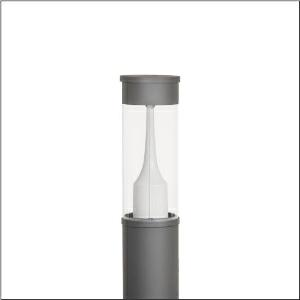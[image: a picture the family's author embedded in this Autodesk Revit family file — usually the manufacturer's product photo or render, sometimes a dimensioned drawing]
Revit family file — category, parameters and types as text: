
# Revit family: city-light_120_iq___pl1_2s_5xa5285rf14h_2286
name_source: partatom
category: Lighting Fixtures
units: mm (PartAtom-declared; Revit-internal decimal feet)

## family parameters
Cut with Voids When Loaded = No
Host = Face
Light Source = No
Part Type = Normal
Room Calculation Point = No
Round Connector Dimension = Use Diameter
Shared = No

## types (1)
- --- (1 x LED, 2970 lm, 18.5 W, 4000K)
    Apparent Load = 19 VA
    CIE Flux Codes = 23 62 94 96 100
    Color Rendering = 70
    Color Temperature = 4000K
    Default Elevation = 1800 mm
    Description = City-Light 120 iQ, bollard luminaire, Module 540 iQ-SR, primary light control with 3 zone facetted reflector, of plastic, silver coated, highly specular, structured, primary optical cover: cover, of PMMA, transparent, partly coated, light distribution: PL1.2s, primary light characteristic: symmetric, LED, High Power LED, rated luminous flux: 2.970lm, luminous efficacy: 161lm/W, light colour: 740, colour temperature: 4000K, control gear: iQ Street-Remote, control: pre-setting: logarithmic dimming characteristic, Street-Remote, Auto-Match, Temp-Guard, Lumen-Switch, Night-Set, Smart-Wire, Light-Fading, Desk-Remote (wireless, voltage-free reading and setting of iQ features in the workshop via application-optimized NFC function/RFID function), optimised constant luminous flux control (CLO 2.0), with terminal, 6-pole, max. 2.5mm², mains connection: 230..240V, AC, 50/60Hz, start of lifetime: 19W, end of service life: 20W, reduction: 9W, luminaire housing, cylindrical, of extruded aluminium section, coated, Siteco® metallic grey (DB 702S), length: 1.200mm, diameter: 200mm, Module 540 iQ-SR, traffic white (RAL 9016), equipment: standard, protection rating (complete): IP54, insulation class (complete): insulation class II (safety insulation), certification: CE, ENEC, VDE, packaging unit: 1 piece

Light Distribution: PL1.2s
    Height = 500 mm
    Lamp = 1 x LED
    Lamp Light Flux = 2970 lm
    Lamp Power = 18.5 W
    Lamp count = 1
    Length = 200 mm  [stored 0.656168 ft]
    Luminous efficacy = 161 lm/W
    Manufacturer = Siteco
    ModVariant = No
    Model = 5XA5285RF14H
    Mounting Place = Floor
    Mounting Type = Freestanding
    Number of Poles = 1
    OnlyDefault = Yes
    Power Factor = 1
    Product Name = City-Light 120 iQ | PL1.2s
    Product group = bollard luminaire
    ProductGroupID = 1304
    Protection Class = Protection class II
    Protection Degree = IP 54
    RLX_Detail_Level = 1
    RLX_Emergency_Light_Flux = 0 lm
    RLX_Emergency_Type = 0
    RLX_Emergency_Type_DB = No
    RlxData = <blob elided: 30413 chars, md5=b889f6f8>
    Socket = socket
    Standby Power = 0 W
    System Light Flux = 2970 lm
    System Power = 19 W
    Type Comments = factory setting: luminous flux: 100 % | dim-lin: 254 | 385 mA
    Type Image = l_1006922.jpg
    URL = http://relux.com
    VarID = @adj_146209
    Voltage = 0 V
    Weight = 0.00 kg
    Width = 0 mm  [stored 0 ft]

note: [stored X ft] marks values corroborated as IEEE doubles in the binary element streams (Revit-internal decimal feet)

## geometry (parser evidence)
native form markers: Blend x4, Sweep x12
no freeform markers — native parametric forms only
